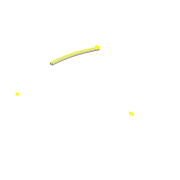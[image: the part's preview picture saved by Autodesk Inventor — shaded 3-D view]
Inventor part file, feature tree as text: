
AUTODESK INVENTOR PART (.ipt)
format: ipt  version: 2022 (Build 260153000, 153)  size: 127,488 bytes
history: native  units: mm
features: sketch x4, extrude x2, projected_geometry x2, fillet x1
ambient origin geometry x8: Origin, YZ Plane, XZ Plane, XY Plane, X Axis, Y Axis, Z Axis, Center Point
bodies: Solid1 (feature_tree)
feature tree (9):
  extrude  "Extrusion1"  Depth=10.0mm
  fillet  "Fillet1"  Radius=3.0mm
  sketch  "Sketch2"  dims[d3=3.0mm d4=8.0mm d5=0.0mm]
  extrude  "Extrusion2"  Depth=8.0mm TaperAngle=0.0deg
  sketch  "Sketch4"  dims[d13=400.0mm d14=2.0mm d15=30.0mm d16=180.0mm d17=190.354919mm d18=20.0mm d19=0.0mm]
  sketch  "Sketch1"  dims[d0=382.775mm d1=10.0mm d2=3.0mm]
  projected_geometry  "Projected Loop1"
  sketch  "Sketch3"  dims[d12=400.0mm]
  projected_geometry  "Projected Loop2"
